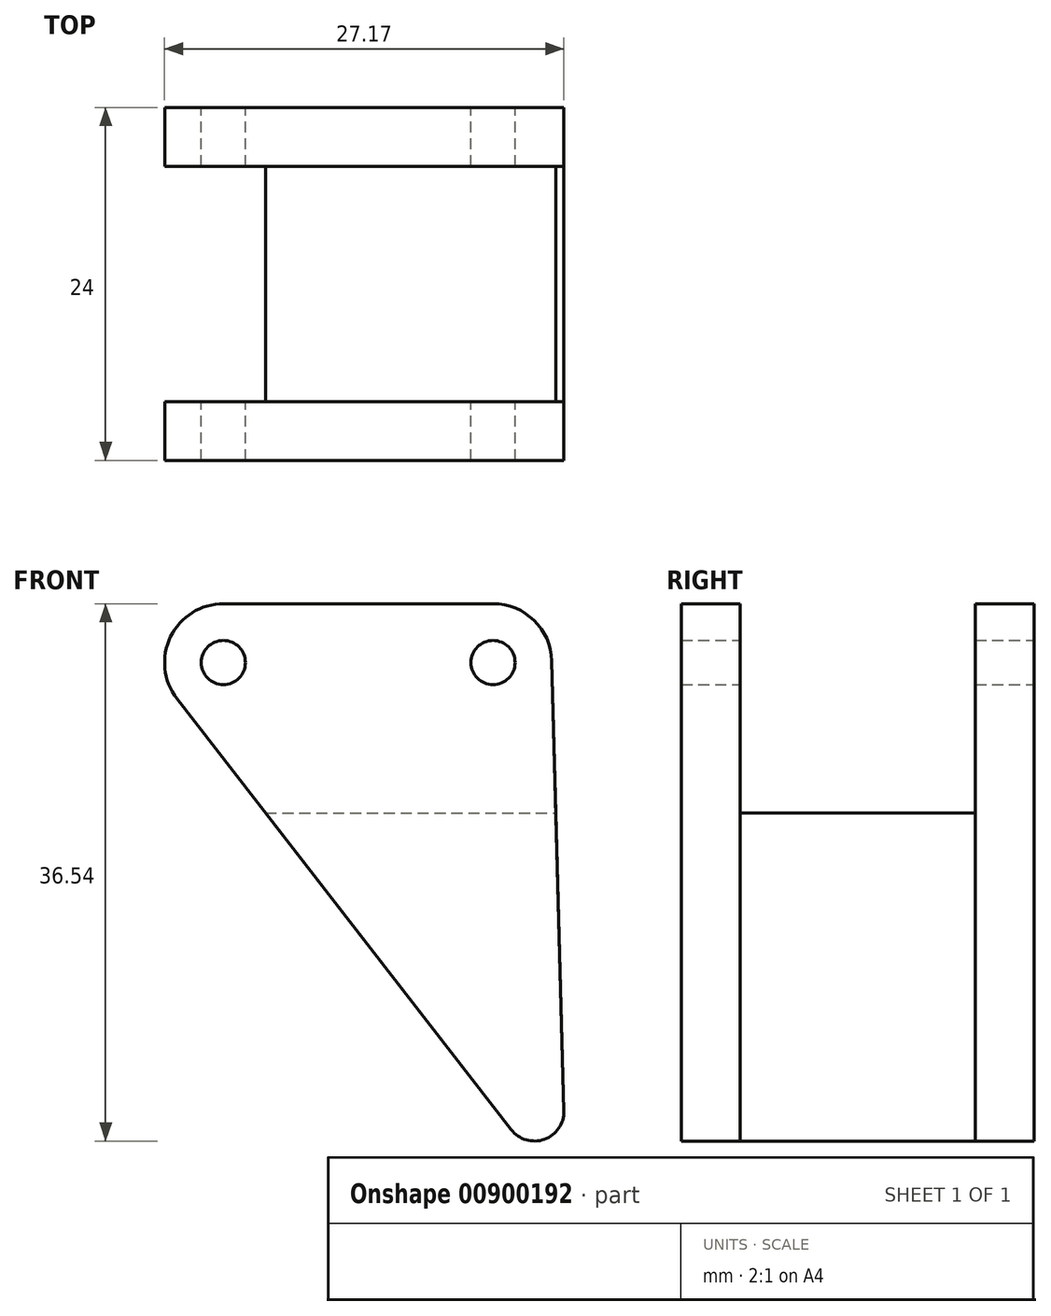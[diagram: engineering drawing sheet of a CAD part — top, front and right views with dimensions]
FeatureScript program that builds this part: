
annotation { "Feature Type Name" : "Feature", "Feature Type Description" : "" }
export const myFeature = defineFeature(function(context is Context, id is Id, definition is map)
    precondition{}
    {
        {
            var Q0;
            Q0=qCreatedBy(makeId("Front.planeOp"),FACE);
            var sketch = newSketch(context, id + "F0", { "sketchPlane" : qUnion([Q0])});
            skLineSegment(sketch, "E0", {"start": v(-24.33, 28.09) * mm, "end": v(-1.58, -1.23) * mm});
            skLineSegment(sketch, "E1", {"start": v(2, 0.05) * mm, "end": v(1.18, 30.65) * mm});
            skLineSegment(sketch, "E2", {"start": v(-2.82, 34.54) * mm, "end": v(-21.17, 34.54) * mm});
            skPoint(sketch, "E3.visualSharp", {"position": v(-29.33, 34.54) * mm});
            skArc(sketch, "E3.filletArc", {"start": v(-21.17, 34.54) * mm, "mid": v(-24.76, 32.3) * mm, "end": v(-24.33, 28.09) * mm});
            skPoint(sketch, "E4.visualSharp", {"position": v(1.08, 34.54) * mm});
            skArc(sketch, "E4.filletArc", {"start": v(1.18, 30.65) * mm, "mid": v(-0.03, 33.4) * mm, "end": v(-2.82, 34.54) * mm});
            skPoint(sketch, "E5.visualSharp", {"position": v(2.16, -6.05) * mm});
            skArc(sketch, "E5.filletArc", {"start": v(-1.58, -1.23) * mm, "mid": v(0.67, -1.88) * mm, "end": v(2, 0.05) * mm});
            skCircle(sketch, "E6", {"center": v(-2.82, 30.54) * mm, "radius": 1.5 * mm});
            skCircle(sketch, "E7", {"center": v(-21.17, 30.54) * mm, "radius": 1.5 * mm});
            skSolve(sketch);
        }
        {
            var Q0;
            Q0 = qSketchRegion(id + "F0", true);
            extrude(context, id + "F1", {"entities" : qUnion([Q0]), "endBound" : BoundingType.SYMMETRIC, "depth" : 24 * mm, "offsetDistance" : 25.4 * mm});
        }
        {
            var Q0;
            Q0=qCreatedBy(makeId("Front.planeOp"),FACE);
            var sketch = newSketch(context, id + "F2", { "sketchPlane" : qUnion([Q0])});
            skLineSegment(sketch, "E8.0.0", {"start": v(2, 0.05) * mm, "end": v(1.18, 30.65) * mm});
            skArc(sketch, "E8.0.1", {"start": v(1.18, 30.65) * mm, "mid": v(-0.03, 33.4) * mm, "end": v(-2.82, 34.54) * mm});
            skLineSegment(sketch, "E8.0.2", {"start": v(-2.82, 34.54) * mm, "end": v(-21.17, 34.54) * mm});
            skArc(sketch, "E8.0.3", {"start": v(-21.17, 34.54) * mm, "mid": v(-24.76, 32.3) * mm, "end": v(-24.33, 28.09) * mm});
            skLineSegment(sketch, "E8.0.4", {"start": v(-24.33, 28.09) * mm, "end": v(-1.58, -1.23) * mm});
            skArc(sketch, "E8.0.5", {"start": v(-1.58, -1.23) * mm, "mid": v(0.67, -1.88) * mm, "end": v(2, 0.05) * mm});
            skSolve(sketch);
        }
        {
            var Q0;
            Q0 = qSketchRegion(id + "F2", true);
            extrude(context, id + "F3", {"entities" : qUnion([Q0]), "operationType" : NewBodyOperationType.REMOVE, "endBound" : BoundingType.SYMMETRIC, "oppositeDirection" : true, "depth" : 16 * mm, "offsetDistance" : 25.4 * mm});
        }
        {
            var Q0;
            Q0=makeQuery(id+"F3.boolean.opBoolean","COPY",FACE,{"derivedFrom":makeQuery(id+"F3.opExtrude","CAP_FACE",FACE,{"disambiguationData":[OSD([sQuery(id+"F2.wireOp",EDGE,"E8.0.0"),sQuery(id+"F2.wireOp",EDGE,"E8.0.1"),sQuery(id+"F2.wireOp",EDGE,"E8.0.2"),sQuery(id+"F2.wireOp",EDGE,"E8.0.3"),sQuery(id+"F2.wireOp",EDGE,"E8.0.4"),sQuery(id+"F2.wireOp",EDGE,"E8.0.5")])],"isStart":false})});
            var sketch = newSketch(context, id + "F4", { "sketchPlane" : qUnion([Q0])});
            skLineSegment(sketch, "E9.0.0", {"start": v(2, 0.05) * mm, "end": v(1.18, 30.65) * mm});
            skArc(sketch, "E9.0.1", {"start": v(1.18, 30.65) * mm, "mid": v(-0.03, 33.4) * mm, "end": v(-2.82, 34.54) * mm});
            skArc(sketch, "E9.0.3", {"start": v(-21.17, 34.54) * mm, "mid": v(-24.76, 32.3) * mm, "end": v(-24.33, 28.09) * mm});
            skLineSegment(sketch, "E9.0.4", {"start": v(-24.33, 28.09) * mm, "end": v(-1.58, -1.23) * mm});
            skArc(sketch, "E9.0.5", {"start": v(-1.58, -1.23) * mm, "mid": v(0.67, -1.88) * mm, "end": v(2, 0.05) * mm});
            skLineSegment(sketch, "E10", {"start": v(-18.3, 20.32) * mm, "end": v(1.46, 20.32) * mm});
            skSolve(sketch);
        }
        {
            var Q0;
            Q0 = qSketchRegion(id + "F4", true);
            extrude(context, id + "F5", {"entities" : qUnion([Q0]), "depth" : 16 * mm, "offsetDistance" : 25.4 * mm});
        }
    });
